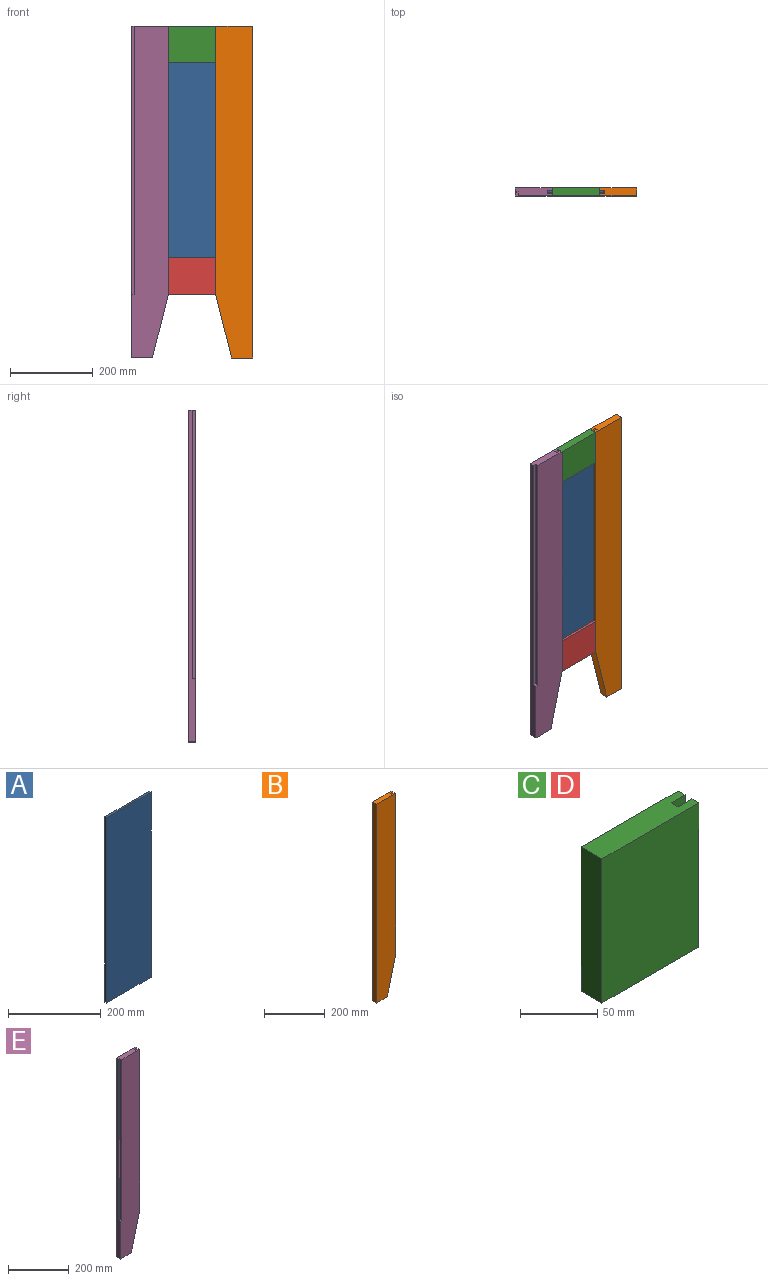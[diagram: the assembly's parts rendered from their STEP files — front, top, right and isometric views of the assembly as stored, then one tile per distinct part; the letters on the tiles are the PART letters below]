
ASSEMBLY  parts=5 mates=4
PART A: 6 faces, bbox 136.5x5.1x489 mm
  f0: plane 136.53x5.08mm, normal (0,0,1), area 693.5mm2, adj f1,f3,f4,f5
  f1: plane 488.95x5.08mm, normal (-1,0,0), area 2483.9mm2, adj f0,f2,f4,f5
  f2: plane 136.53x5.08mm, normal (0,0,-1), area 693.5mm2, adj f1,f3,f4,f5
  f3: plane 488.95x5.08mm, normal (1,0,0), area 2483.9mm2, adj f0,f2,f4,f5
  f4: plane 488.95x136.53mm, normal (0,-1,0), area 66753.9mm2, adj f0,f1,f2,f3
  f5: plane 488.95x136.53mm, normal (0,1,0), area 66753.9mm2, adj f0,f1,f2,f3
PART B: 12 faces, bbox 88.9x19.1x800.1 mm
  f0: plane 647.7x6.35mm, normal (1,0,0), area 4112.9mm2, adj f3,f5,f7,f10
  f1: plane 50.8x19.05mm, normal (0,0,-1), area 967.7mm2, adj f2,f3,f6,f7
  f2: plane 800.1x88.9mm, normal (0,-1,0), area 68225.7mm2, adj f1,f4,f5,f6,f7
  f3: plane 800.1x88.9mm, normal (0,1,0), area 68225.7mm2, adj f0,f1,f5,f6,f7
  f4: plane 647.7x6.35mm, normal (1,0,0), area 4112.9mm2, adj f2,f5,f7,f8
  f5: plane 88.9x19.05mm, normal (0,0,1), area 1612.9mm2, adj f0,f2,f3,f4,f6,f8,f10,f11
  f6: plane 800.1x19.05mm, normal (-1,0,0), area 15241.9mm2, adj f1,f2,f3,f5
  f7: plane 152.4x38.1mm, normal (0.97,0,-0.24), area 2992.6mm2, adj f0,f1,f2,f3,f4,f9
  f8: plane 647.7x12.7mm, normal (0,1,0), area 8225.8mm2, adj f4,f5,f9,f11
  f9: plane 12.7x6.35mm, normal (0,0,1), area 80.6mm2, adj f7,f8,f10,f11
  f10: plane 647.7x12.7mm, normal (0,-1,0), area 8225.8mm2, adj f0,f5,f9,f11
  f11: plane 647.7x6.35mm, normal (1,0,0), area 4112.9mm2, adj f5,f8,f9,f10
PART C: 10 faces, bbox 88.9x19.1x114.3 mm
  f0: plane 114.3x6.35mm, normal (1,0,0), area 725.8mm2, adj f1,f3,f5,f7
  f1: plane 88.9x19.05mm, normal (0,0,-1), area 1612.9mm2, adj f0,f2,f4,f5,f6,f7,f8,f9
  f2: plane 114.3x6.35mm, normal (1,0,0), area 725.8mm2, adj f1,f3,f6,f8
  f3: plane 88.9x19.05mm, normal (0,0,1), area 1612.9mm2, adj f0,f2,f4,f5,f6,f7,f8,f9
  f4: plane 114.3x19.05mm, normal (-1,0,0), area 2177.4mm2, adj f1,f3,f5,f6
  f5: plane 114.3x88.9mm, normal (0,-1,0), area 10161.3mm2, adj f0,f1,f3,f4
  f6: plane 114.3x88.9mm, normal (0,1,0), area 10161.3mm2, adj f1,f2,f3,f4
  f7: plane 114.3x12.7mm, normal (0,1,0), area 1451.6mm2, adj f0,f1,f3,f9
  f8: plane 114.3x12.7mm, normal (0,-1,0), area 1451.6mm2, adj f1,f2,f3,f9
  f9: plane 114.3x6.35mm, normal (1,0,0), area 725.8mm2, adj f1,f3,f7,f8
PART D: same geometry as C
PART E: 15 faces, bbox 88.9x19.1x800.1 mm
  f0: plane 800.1x19.05mm, normal (-1,0,0), area 9072.6mm2, adj f2,f3,f4,f6,f12,f14
  f1: plane 647.7x6.35mm, normal (1,0,0), area 4112.9mm2, adj f4,f6,f7,f10
  f2: plane 50.8x19.05mm, normal (0,0,-1), area 967.7mm2, adj f0,f3,f4,f7
  f3: plane 800.1x88.9mm, normal (0,-1,0), area 64112.8mm2, adj f0,f2,f5,f6,f7,f12,f13
  f4: plane 800.1x88.9mm, normal (0,1,0), area 68225.7mm2, adj f0,f1,f2,f6,f7
  f5: plane 647.7x6.35mm, normal (1,0,0), area 4112.9mm2, adj f3,f6,f7,f8
  f6: plane 88.9x19.05mm, normal (0,0,1), area 1552.4mm2, adj f0,f1,f3,f4,f5,f8,f10,f11
  f7: plane 152.4x38.1mm, normal (0.97,0,-0.24), area 2992.6mm2, adj f1,f2,f3,f4,f5,f9
  f8: plane 647.7x12.7mm, normal (0,1,0), area 8225.8mm2, adj f5,f6,f9,f11
  f9: plane 12.7x6.35mm, normal (0,0,1), area 80.6mm2, adj f7,f8,f10,f11
  f10: plane 647.7x12.7mm, normal (0,-1,0), area 8225.8mm2, adj f1,f6,f9,f11
  f11: plane 647.7x6.35mm, normal (1,0,0), area 4112.9mm2, adj f6,f8,f9,f10
  f12: plane 9.53x6.35mm, normal (0,0,1), area 60.5mm2, adj f0,f3,f13,f14
  f13: plane 647.7x9.53mm, normal (-1,0,0), area 6169.3mm2, adj f3,f6,f12,f14
  f14: plane 647.7x6.35mm, normal (0,-1,0), area 4112.9mm2, adj f0,f6,f12,f13
PLACE A t=(790.63,-402.6,81.26)mm
PLACE B rot(axis=(0,0,1),180deg) t=(893.82,-402.6,5.06)mm
PLACE C rot(axis=(0,1,0),90deg) t=(792.22,-402.6,360.66)mm
PLACE D rot(axis=(-0.71,0,-0.71),180deg) t=(792.22,-402.6,-198.14)mm
PLACE E t=(690.62,-402.6,5.06)mm
MATE fastened E.f11 <-> A.f1  axis (1,0,0) through (722.37,-402.6,81.26)mm
MATE fastened E.f5 <-> D.f1  axis (1,0,0) through (735.07,-412.13,-242.59)mm
MATE fastened C.f1 <-> E.f5  axis (-1,0,0) through (735.07,-412.13,405.11)mm
MATE fastened B.f0 <-> C.f3  axis (-1,0,0) through (849.37,-412.13,405.11)mm
